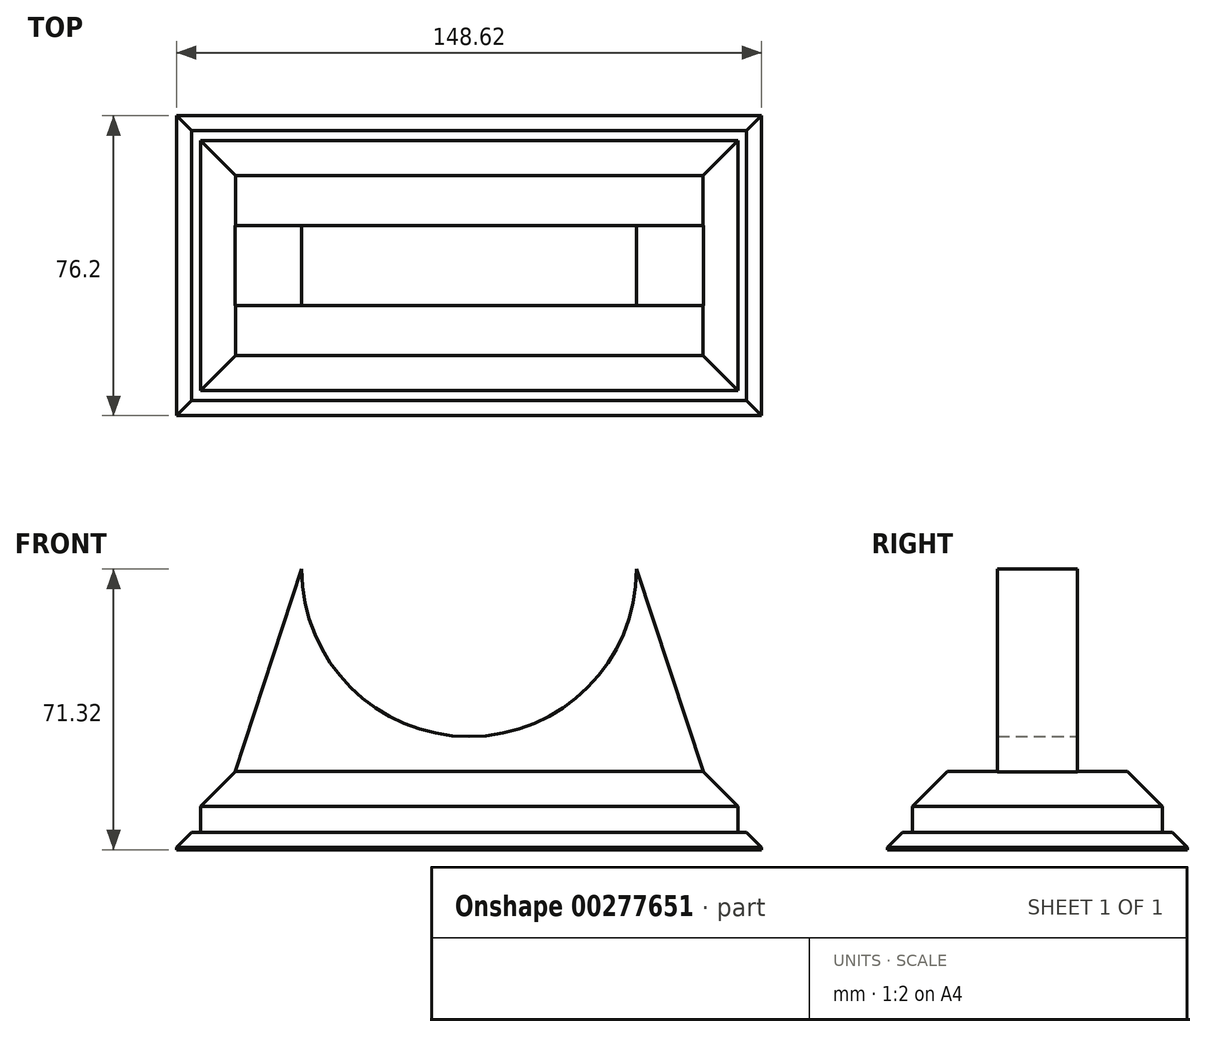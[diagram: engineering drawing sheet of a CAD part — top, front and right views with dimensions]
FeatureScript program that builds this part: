
annotation { "Feature Type Name" : "Feature", "Feature Type Description" : "" }
export const myFeature = defineFeature(function(context is Context, id is Id, definition is map)
    precondition{}
    {
        {
            var Q0;
            Q0=qCreatedBy(makeId("Front.planeOp"),FACE);
            var sketch = newSketch(context, id + "F0", { "sketchPlane" : qUnion([Q0])});
            skCircle(sketch, "E0", {"center": v(0, 0) * mm, "radius": 42.55 * mm});
            skLineSegment(sketch, "E1", {"start": v(-42.55, 0) * mm, "end": v(-59.45, -51.4) * mm});
            skLineSegment(sketch, "E2", {"start": v(-59.45, -51.4) * mm, "end": v(0, -51.4) * mm});
            skLineSegment(sketch, "E3.bottom", {"start": v(-68.26, -51.4) * mm, "end": v(0, -51.4) * mm});
            skLineSegment(sketch, "E3.top", {"start": v(-68.26, -66.92) * mm, "end": v(0, -66.92) * mm});
            skLineSegment(sketch, "E3.left", {"start": v(-68.26, -51.4) * mm, "end": v(-68.26, -66.92) * mm});
            skLineSegment(sketch, "E3.right", {"start": v(0, -51.4) * mm, "end": v(0, -66.92) * mm});
            skLineSegment(sketch, "E4.MirrorCS", {"start": v(42.55, 0) * mm, "end": v(59.45, -51.4) * mm});
            skLineSegment(sketch, "E5.MirrorCS", {"start": v(68.26, -51.4) * mm, "end": v(0, -51.4) * mm});
            skLineSegment(sketch, "E6.MirrorCS", {"start": v(68.26, -51.4) * mm, "end": v(68.26, -66.92) * mm});
            skLineSegment(sketch, "E7.MirrorCS", {"start": v(68.26, -66.92) * mm, "end": v(0, -66.92) * mm});
            skLineSegment(sketch, "E8.bottom", {"start": v(-74.31, -66.92) * mm, "end": v(0, -66.92) * mm});
            skLineSegment(sketch, "E8.top", {"start": v(-74.31, -71.32) * mm, "end": v(0, -71.32) * mm});
            skLineSegment(sketch, "E8.left", {"start": v(-74.31, -66.92) * mm, "end": v(-74.31, -71.32) * mm});
            skLineSegment(sketch, "E8.right", {"start": v(0, -66.92) * mm, "end": v(0, -71.32) * mm});
            skLineSegment(sketch, "E9.MirrorCS", {"start": v(74.31, -71.32) * mm, "end": v(0, -71.32) * mm});
            skLineSegment(sketch, "E10.MirrorCS", {"start": v(74.31, -66.92) * mm, "end": v(74.31, -71.32) * mm});
            skLineSegment(sketch, "E11.MirrorCS", {"start": v(74.31, -66.92) * mm, "end": v(0, -66.92) * mm});
            skSolve(sketch);
        }
        {
            var Q0;
            {var subQ2=sQuery(id+"F0.wireOp",EDGE,"E1");Q0=makeQuery(id+"F0.imprint","IMPRINT",FACE,{"disambiguationData":[TD([[makeQuery(id+"F0.imprint","IMPRINT",EDGE,{"derivedFrom":subQ2}),1.0]])]});}
            extrude(context, id + "F1", {"entities" : qUnion([Q0]), "endBound" : BoundingType.SYMMETRIC, "depth" : 20.32 * mm});
        }
        {
            var Q0;
            {var subQ1=sQuery(id+"F0.wireOp",EDGE,"E3.left");Q0=makeQuery(id+"F0.imprint","IMPRINT",FACE,{"disambiguationData":[TD([[makeQuery(id+"F0.imprint","IMPRINT",EDGE,{"derivedFrom":subQ1}),1.0]])]});}
            var Q1;
            {var subQ2=sQuery(id+"F0.wireOp",EDGE,"E3.right");Q1=makeQuery(id+"F0.imprint","IMPRINT",FACE,{"disambiguationData":[TD([[makeQuery(id+"F0.imprint","IMPRINT",EDGE,{"derivedFrom":subQ2}),1.0]])]});}
            extrude(context, id + "F2", {"entities" : qUnion([Q0, Q1]), "operationType" : NewBodyOperationType.ADD, "endBound" : BoundingType.SYMMETRIC, "depth" : 63.5 * mm});
        }
        {
            var Q0;
            {var subQ3=sQuery(id+"F0.wireOp",EDGE,"E8.right");Q0=makeQuery(id+"F0.imprint","IMPRINT",FACE,{"disambiguationData":[TD([[makeQuery(id+"F0.imprint","IMPRINT",EDGE,{"derivedFrom":subQ3}),1.0]])]});}
            var Q1;
            Q1=makeQuery(id+"F0.imprint","IMPRINT",FACE,{"disambiguationData":[TD([[makeQuery(id+"F0.imprint","IMPRINT",EDGE,{"derivedFrom":sQuery(id+"F0.wireOp",EDGE,"E8.top")}),1.0]])]});
            extrude(context, id + "F3", {"entities" : qUnion([Q0, Q1]), "operationType" : NewBodyOperationType.ADD, "endBound" : BoundingType.SYMMETRIC, "depth" : 76.2 * mm});
        }
        {
            var Q0;
            Q0=makeQuery(id+"F2.opExtrude","CAP_EDGE",EDGE,{"disambiguationData":[OSD([sQuery(id+"F0.wireOp",EDGE,"E3.bottom"),sQuery(id+"F0.wireOp",EDGE,"E5.MirrorCS")])],"isStart":false});
            var Q1;
            Q1=makeQuery(id+"F2.opExtrude","SWEPT_EDGE",EDGE,{"disambiguationData":[OSD([sQuery(id+"F0.wireOp",EDGE,"E5.MirrorCS"),sQuery(id+"F0.wireOp",EDGE,"E6.MirrorCS")])]});
            var Q2;
            Q2=makeQuery(id+"F2.opExtrude","CAP_EDGE",EDGE,{"disambiguationData":[OSD([sQuery(id+"F0.wireOp",EDGE,"E3.bottom"),sQuery(id+"F0.wireOp",EDGE,"E5.MirrorCS")])],"isStart":true});
            var Q3;
            Q3=makeQuery(id+"F2.opExtrude","SWEPT_EDGE",EDGE,{"disambiguationData":[OSD([sQuery(id+"F0.wireOp",EDGE,"E3.bottom"),sQuery(id+"F0.wireOp",EDGE,"E3.left")])]});
            chamfer(context, id + "F4", {"entities" : qUnion([Q0, Q1, Q2, Q3]), "width" : 8.9 * mm, "tangentPropagation" : true});
        }
        {
            var Q0;
            Q0=makeQuery(id+"F3.opExtrude","CAP_EDGE",EDGE,{"disambiguationData":[OSD([sQuery(id+"F0.wireOp",EDGE,"E8.bottom"),sQuery(id+"F0.wireOp",EDGE,"E11.MirrorCS")])],"isStart":false});
            var Q1;
            Q1=makeQuery(id+"F3.opExtrude","SWEPT_EDGE",EDGE,{"disambiguationData":[OSD([sQuery(id+"F0.wireOp",EDGE,"E8.bottom"),sQuery(id+"F0.wireOp",EDGE,"E8.left")])]});
            var Q2;
            Q2=makeQuery(id+"F3.opExtrude","SWEPT_EDGE",EDGE,{"disambiguationData":[OSD([sQuery(id+"F0.wireOp",EDGE,"E10.MirrorCS"),sQuery(id+"F0.wireOp",EDGE,"E11.MirrorCS")])]});
            var Q3;
            Q3=makeQuery(id+"F3.opExtrude","CAP_EDGE",EDGE,{"disambiguationData":[OSD([sQuery(id+"F0.wireOp",EDGE,"E8.bottom"),sQuery(id+"F0.wireOp",EDGE,"E11.MirrorCS")])],"isStart":true});
            chamfer(context, id + "F5", {"entities" : qUnion([Q0, Q1, Q2, Q3]), "width" : 3.8 * mm, "tangentPropagation" : true});
        }
    });
